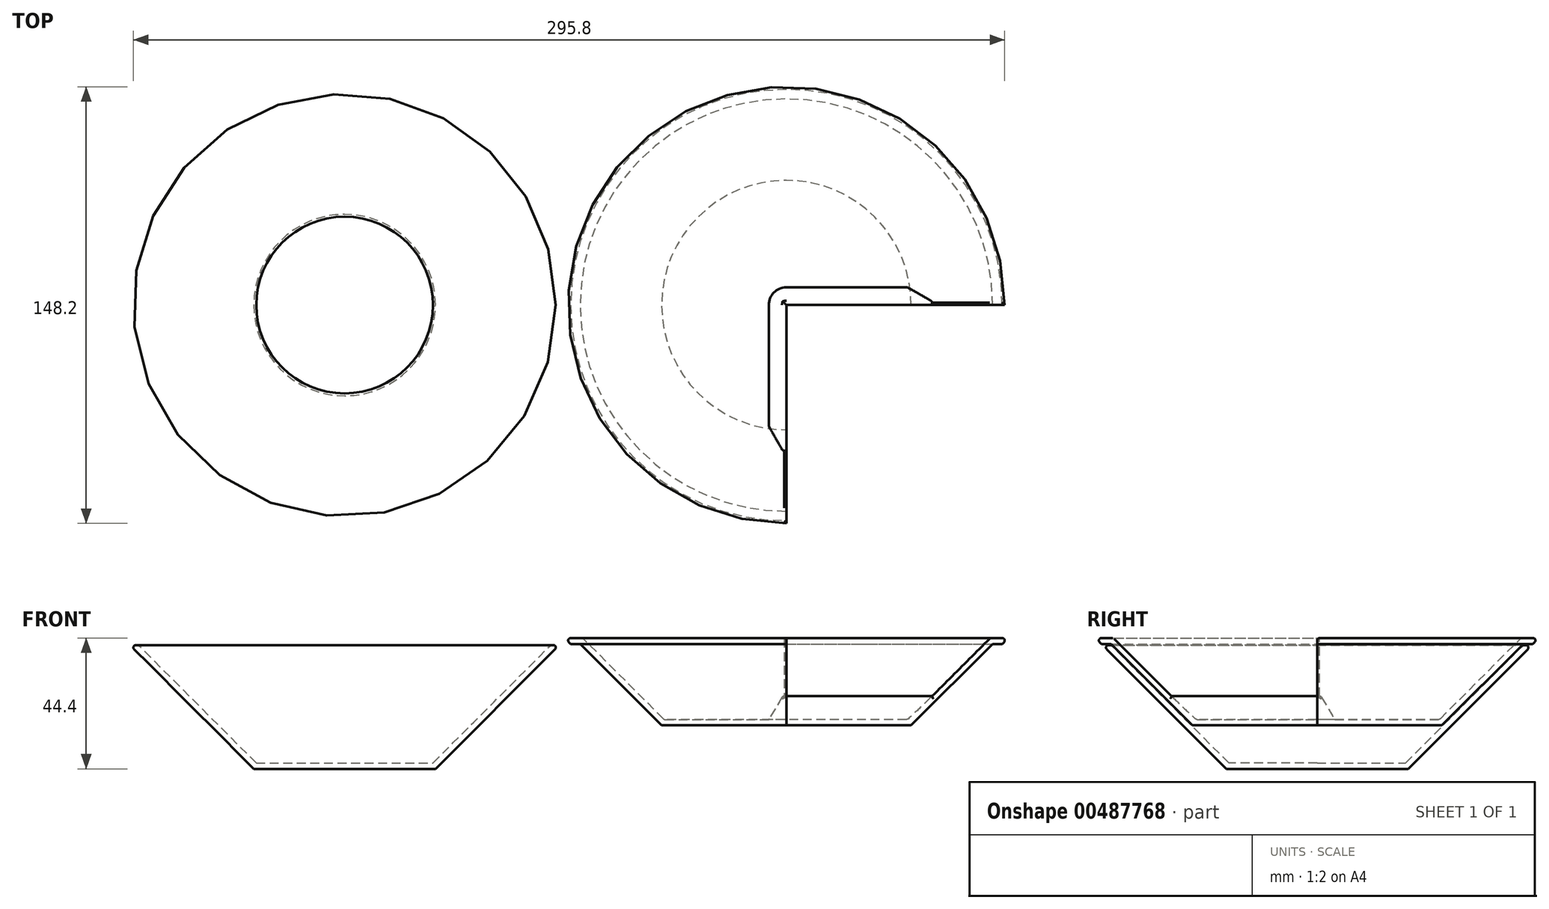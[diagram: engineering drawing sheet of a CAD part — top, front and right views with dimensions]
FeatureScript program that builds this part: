
annotation { "Feature Type Name" : "Feature", "Feature Type Description" : "" }
export const myFeature = defineFeature(function(context is Context, id is Id, definition is map)
    precondition{}
    {
        {
            var Q0;
            Q0=qCreatedBy(makeId("Front.planeOp"),FACE);
            var sketch = newSketch(context, id + "F0", { "sketchPlane" : qUnion([Q0])});
            skLineSegment(sketch, "E0", {"start": v(0, 0) * mm, "end": v(30, 0) * mm});
            skLineSegment(sketch, "E1", {"start": v(30, 0) * mm, "end": v(70, 40) * mm});
            skLineSegment(sketch, "E2", {"start": v(0, 0) * mm, "end": v(0, 40) * mm, "construction": true});
            skLineSegment(sketch, "E3.0", {"start": v(30.83, -2) * mm, "end": v(48.05, 15.23) * mm});
            skLineSegment(sketch, "E3.1", {"start": v(0, -2) * mm, "end": v(30.83, -2) * mm});
            skLineSegment(sketch, "E4", {"start": v(48.05, 15.23) * mm, "end": v(72.83, 40) * mm});
            skLineSegment(sketch, "E5", {"start": v(72.83, 40) * mm, "end": v(70, 40) * mm});
            skLineSegment(sketch, "E6", {"start": v(0, -2) * mm, "end": v(0, 0) * mm});
            skSolve(sketch);
        }
        {
            var Q0;
            Q0=makeQuery(id+"F0.imprint","IMPRINT",FACE,{"disambiguationData":[TD([[makeQuery(id+"F0.imprint","IMPRINT",EDGE,{"derivedFrom":sQuery(id+"F0.wireOp",EDGE,"E0")}),-1.0]])]});
            var Q1;
            Q1=sQuery(id+"F0.wireOp",EDGE,"E2");
            revolve(context, id + "F1", {"entities" : qUnion([Q0]), "axis" : qUnion([Q1]), "revolveType" : RevolveType.FULL});
        }
        {
            var Q0;
            Q0=qCreatedBy(makeId("Front.planeOp"),FACE);
            var sketch = newSketch(context, id + "F2", { "sketchPlane" : qUnion([Q0])});
            skLineSegment(sketch, "E7.0", {"start": v(30, 0) * mm, "end": v(70, 40) * mm, "construction": true});
            skLineSegment(sketch, "E7.1", {"start": v(72.83, 40) * mm, "end": v(70, 40) * mm, "construction": true});
            skLineSegment(sketch, "E7.2", {"start": v(48.05, 15.23) * mm, "end": v(72.83, 40) * mm, "construction": true});
            skLineSegment(sketch, "E7.3", {"start": v(30.83, -2) * mm, "end": v(48.05, 15.23) * mm, "construction": true});
            skLineSegment(sketch, "E7.4", {"start": v(0, -2) * mm, "end": v(30.83, -2) * mm, "construction": true});
            skLineSegment(sketch, "E7.5", {"start": v(0, -2) * mm, "end": v(0, 0) * mm, "construction": true});
            skLineSegment(sketch, "E7.6.0", {"start": v(0, -2) * mm, "end": v(30.83, -2) * mm, "construction": true});
            skLineSegment(sketch, "E7.6.1", {"start": v(30.83, -2) * mm, "end": v(48.05, 15.23) * mm, "construction": true});
            skLineSegment(sketch, "E7.6.2", {"start": v(48.05, 15.23) * mm, "end": v(72.83, 40) * mm, "construction": true});
            skLineSegment(sketch, "E7.6.3", {"start": v(72.83, 40) * mm, "end": v(70, 40) * mm, "construction": true});
            skLineSegment(sketch, "E7.6.4", {"start": v(70, 40) * mm, "end": v(30, 0) * mm, "construction": true});
            skLineSegment(sketch, "E7.6.5", {"start": v(30, 0) * mm, "end": v(0, 0) * mm, "construction": true});
            skLineSegment(sketch, "E7.6.6", {"start": v(0, 0) * mm, "end": v(0, -2) * mm, "construction": true});
            skLineSegment(sketch, "E8", {"start": v(69.6, 40) * mm, "end": v(42.36, 12.76) * mm});
            skLineSegment(sketch, "E9", {"start": v(42.36, 12.76) * mm, "end": v(0, 12.76) * mm});
            skLineSegment(sketch, "E10", {"start": v(0, 12.76) * mm, "end": v(0, 14.76) * mm});
            skLineSegment(sketch, "E11", {"start": v(61.54, 34.76) * mm, "end": v(41.54, 14.76) * mm});
            skLineSegment(sketch, "E12", {"start": v(41.54, 14.76) * mm, "end": v(0, 14.76) * mm});
            skLineSegment(sketch, "E13", {"start": v(61.54, 34.76) * mm, "end": v(69.17, 42.4) * mm});
            skLineSegment(sketch, "E14", {"start": v(69.17, 42.4) * mm, "end": v(75.23, 42.4) * mm});
            skLineSegment(sketch, "E15", {"start": v(69.6, 40) * mm, "end": v(70, 40.4) * mm});
            skLineSegment(sketch, "E16", {"start": v(70, 40.4) * mm, "end": v(73.23, 40.4) * mm});
            skLineSegment(sketch, "E17", {"start": v(73.23, 40.4) * mm, "end": v(75.23, 42.4) * mm});
            skLineSegment(sketch, "E18", {"start": v(72.83, 40) * mm, "end": v(73.23, 40.4) * mm, "construction": true});
            skSolve(sketch);
        }
        {
            var Q0;
            Q0 = qSketchRegion(id + "F2", true);
            var Q1;
            Q1=sQuery(id+"F2.wireOp",EDGE,"E10");
            revolve(context, id + "F3", {"entities" : qUnion([Q0]), "axis" : qUnion([Q1]), "revolveType" : RevolveType.ONE_DIRECTION, "angle" : 270 * degree});
        }
        {
            var Q0;
            Q0=qCreatedBy(makeId("Front.planeOp"),FACE);
            var sketch = newSketch(context, id + "F4", { "sketchPlane" : qUnion([Q0])});
            skPoint(sketch, "E19.0", {"position": v(0, 14.76) * mm});
            skLineSegment(sketch, "E19.1", {"start": v(0, 12.76) * mm, "end": v(0, 14.76) * mm, "construction": true});
            skLineSegment(sketch, "E20", {"start": v(0, 14.76) * mm, "end": v(0, 24.76) * mm});
            skLineSegment(sketch, "E21", {"start": v(0, 24.76) * mm, "end": v(-6, 14.76) * mm});
            skLineSegment(sketch, "E22", {"start": v(-6, 14.76) * mm, "end": v(0, 14.76) * mm});
            skSolve(sketch);
        }
        {
            var Q0;
            Q0=makeQuery(id+"F4.imprint","IMPRINT",FACE,{"disambiguationData":[TD([[makeQuery(id+"F4.imprint","IMPRINT",EDGE,{"derivedFrom":sQuery(id+"F4.wireOp",EDGE,"E20")}),1.0]])]});
            var Q1;
            Q1=sQuery(id+"F4.wireOp",EDGE,"E20");
            revolve(context, id + "F5", {"operationType" : NewBodyOperationType.ADD, "entities" : qUnion([Q0]), "axis" : qUnion([Q1]), "revolveType" : RevolveType.ONE_DIRECTION, "oppositeDirection" : true, "angle" : 90 * degree});
        }
        {
            var Q0;
            Q0=makeQuery(id+"F5.opRevolve","CAP_FACE",FACE,{"disambiguationData":[OSD([sQuery(id+"F4.wireOp",EDGE,"E20"),sQuery(id+"F4.wireOp",EDGE,"E21"),sQuery(id+"F4.wireOp",EDGE,"E22")])],"isStart":false});
            var Q1;
            Q1=makeQuery(id+"F3.opRevolve","SWEPT_FACE",FACE,{"disambiguationData":[OSD([sQuery(id+"F2.wireOp",EDGE,"E11")])]});
            extrude(context, id + "F6", {"entities" : qUnion([Q0]), "operationType" : NewBodyOperationType.ADD, "endBound" : BoundingType.UP_TO_SURFACE, "endBoundEntityFace" : qUnion([Q1]), "depth" : 25 * mm});
        }
        {
            var Q0;
            Q0 = qSketchRegion(id + "F4", true);
            var Q1;
            Q1=makeQuery(id+"F3.opRevolve","SWEPT_FACE",FACE,{"disambiguationData":[OSD([sQuery(id+"F2.wireOp",EDGE,"E11")])]});
            extrude(context, id + "F7", {"entities" : qUnion([Q0]), "operationType" : NewBodyOperationType.ADD, "endBound" : BoundingType.UP_TO_SURFACE, "endBoundEntityFace" : qUnion([Q1]), "depth" : 25 * mm});
        }
        {
            var Q0;
            Q0=makeQuery(id+"F1.opRevolve","SWEPT_EDGE",EDGE,{"disambiguationData":[OSD([sQuery(id+"F0.wireOp",EDGE,"E4"),sQuery(id+"F0.wireOp",EDGE,"E5")])]});
            var Q1;
            Q1=makeQuery(id+"F1.opRevolve","SWEPT_EDGE",EDGE,{"disambiguationData":[OSD([sQuery(id+"F0.wireOp",EDGE,"E1"),sQuery(id+"F0.wireOp",EDGE,"E5")])]});
            var Q2;
            Q2=makeQuery(id+"F3.opRevolve","SWEPT_EDGE",EDGE,{"disambiguationData":[OSD([sQuery(id+"F2.wireOp",EDGE,"58c1a027-e790-4502-81eb-f8b51346ec1d.0"),sQuery(id+"F2.wireOp",EDGE,"ktVzyKFa-hXeQ-VYO6-rmLh-v9c8zikCZ0W9")])]});
            var Q3;
            Q3=makeQuery(id+"F3.opRevolve","SWEPT_EDGE",EDGE,{"disambiguationData":[OSD([sQuery(id+"F2.wireOp",EDGE,"23296644-c1c2-44d7-abc8-2b32b40eeb05.0"),sQuery(id+"F2.wireOp",EDGE,"ktVzyKFa-hXeQ-VYO6-rmLh-v9c8zikCZ0W9")])]});
            var Q4;
            Q4=makeQuery(id+"F3.opRevolve","SWEPT_EDGE",EDGE,{"disambiguationData":[OSD([sQuery(id+"F2.wireOp",EDGE,"1nYXGZvL-v6C0-AHQH-aAyi-UDgJKJBwxziY"),sQuery(id+"F2.wireOp",EDGE,"E11")])]});
            var Q5;
            Q5=makeQuery(id+"F7.opExtrude","SWEPT_EDGE",EDGE,{"disambiguationData":[OSD([sQuery(id+"F4.wireOp",EDGE,"E20"),sQuery(id+"F4.wireOp",EDGE,"E21")])]});
            var Q6;
            Q6=makeQuery(id+"F6.opExtrude","SWEPT_EDGE",EDGE,{"disambiguationData":[OSD([sQuery(id+"F4.wireOp",EDGE,"E20"),sQuery(id+"F4.wireOp",EDGE,"E21")])]});
            var Q7;
            Q7=makeQuery(id+"F3.opRevolve","CAP_EDGE",EDGE,{"disambiguationData":[OSD([sQuery(id+"F2.wireOp",EDGE,"E11")])],"isStart":true});
            var Q8;
            Q8=makeQuery(id+"F3.opRevolve","CAP_EDGE",EDGE,{"disambiguationData":[OSD([sQuery(id+"F2.wireOp",EDGE,"E11")])],"isStart":false});
            var Q9;
            Q9=makeQuery(id+"F3.opRevolve","CAP_EDGE",EDGE,{"disambiguationData":[OSD([sQuery(id+"F2.wireOp",EDGE,"E14")])],"isStart":true});
            var Q10;
            Q10=makeQuery(id+"F3.opRevolve","CAP_EDGE",EDGE,{"disambiguationData":[OSD([sQuery(id+"F2.wireOp",EDGE,"E14")])],"isStart":false});
            var Q11;
            Q11=makeQuery(id+"F3.opRevolve","SWEPT_EDGE",EDGE,{"disambiguationData":[OSD([sQuery(id+"F2.wireOp",EDGE,"E13"),sQuery(id+"F2.wireOp",EDGE,"E14")])]});
            var Q12;
            Q12=makeQuery(id+"F3.opRevolve","SWEPT_EDGE",EDGE,{"disambiguationData":[OSD([sQuery(id+"F2.wireOp",EDGE,"E14"),sQuery(id+"F2.wireOp",EDGE,"E17")])]});
            fillet(context, id + "F8", {"entities" : qUnion([Q0, Q1, Q2, Q3, Q4, Q5, Q6, Q7, Q8, Q9, Q10, Q11, Q12]), "radius" : .8 * mm, "tangentPropagation" : true, "allowEdgeOverflow" : false});
        }
        {
            var Q0;
            Q0=makeQuery(id+"F3.opRevolve","SWEPT_BODY",BODY,{"disambiguationData":[OSD([sQuery(id+"F2.wireOp",EDGE,"E8"),sQuery(id+"F2.wireOp",EDGE,"E9"),sQuery(id+"F2.wireOp",EDGE,"E10"),sQuery(id+"F2.wireOp",EDGE,"E11"),sQuery(id+"F2.wireOp",EDGE,"E12"),sQuery(id+"F2.wireOp",EDGE,"E13"),sQuery(id+"F2.wireOp",EDGE,"E14"),sQuery(id+"F2.wireOp",EDGE,"E15"),sQuery(id+"F2.wireOp",EDGE,"E16"),sQuery(id+"F2.wireOp",EDGE,"E17")])]});
            transform(context, id + "F9", {"entities" : qUnion([Q0]), "transformType" : TransformType.TRANSLATION_3D, "dx" : 150 * mm, "dy" : 0 * mm, "dz" : 0 * mm, "makeCopy" : false});
        }
    });
